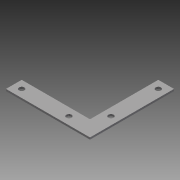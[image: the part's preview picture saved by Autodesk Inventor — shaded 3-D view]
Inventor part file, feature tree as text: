
AUTODESK INVENTOR PART (.ipt)
format: ipt  version: 2015 SP1 (Build 190203100, 203)  size: 109,568 bytes
history: native  units: in
note: dims shown in document units (in); Inventor stores cm internally (conversion verified against a paired STEP export)
features: sketch x2, extrude x1, hole x1
ambient origin geometry x8: Origin, YZ Plane, XZ Plane, XY Plane, X Axis, Y Axis, Z Axis, Center Point
bodies: Solid1 (feature_tree)
feature tree (4):
  extrude  "Extrusion1"  Depth=0.75in
  hole  "Hole1"  [1 undecoded]
  sketch  "Sketch1"  dims[d0=4.0in d1=0.75in]
  sketch  "Sketch2"  dims[d2=0.75in d3=4.0in d4=0.09in d5=0.0in d8=0.375in d11=0.375in d13=0.375in d14=0.375in d16=0.25in d17=0.75in d18=0.375in d19=0.25in d20=0.5635in d21=1.0in d22=0.8108in d23=1.375in d24=3.625in d25=1.375in d26=3.625in]
note: 1 required parameter value undecoded (feature->parameter linkage not recoverable at this tier; creation-order binding heuristic only, values carry confidence <= 0.55)
